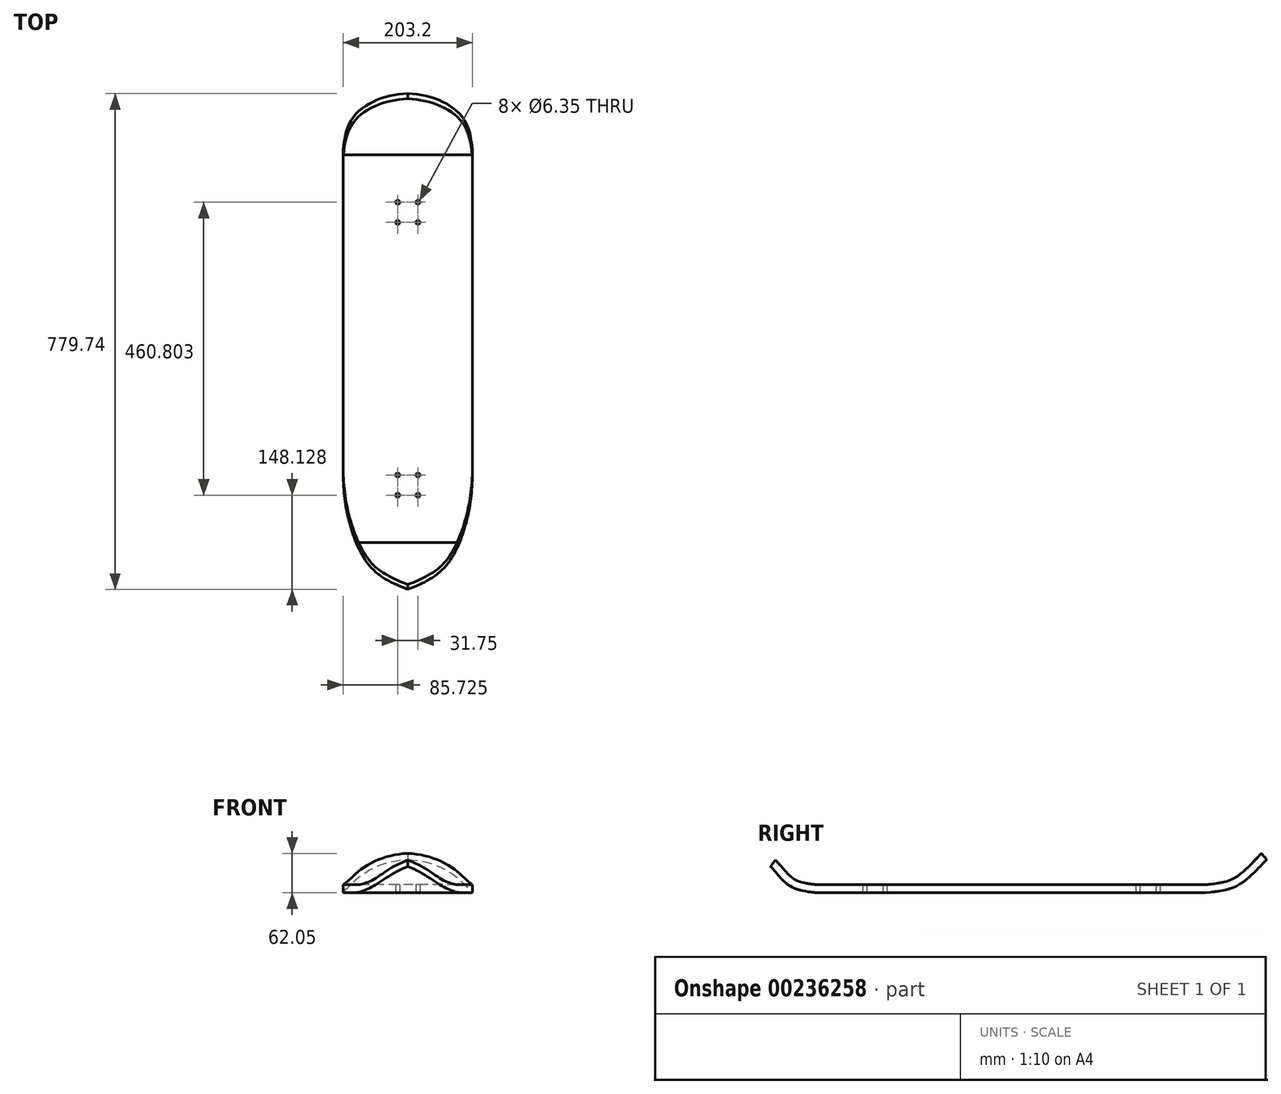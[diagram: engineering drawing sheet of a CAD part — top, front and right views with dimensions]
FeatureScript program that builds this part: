
annotation { "Feature Type Name" : "Feature", "Feature Type Description" : "" }
export const myFeature = defineFeature(function(context is Context, id is Id, definition is map)
    precondition{}
    {
        {
            var Q0;
            Q0=qCreatedBy(makeId("Top.planeOp"),FACE);
            var sketch = newSketch(context, id + "F0", { "sketchPlane" : qUnion([Q0])});
            skLineSegment(sketch, "E0.bottom", {"start": v(101.6, -304.8) * mm, "end": v(-101.6, -304.8) * mm});
            skLineSegment(sketch, "E0.top", {"start": v(101.6, 304.8) * mm, "end": v(-101.6, 304.8) * mm});
            skLineSegment(sketch, "E0.left", {"start": v(101.6, -304.8) * mm, "end": v(101.6, 304.8) * mm});
            skLineSegment(sketch, "E0.right", {"start": v(-101.6, -304.8) * mm, "end": v(-101.6, 304.8) * mm});
            skPoint(sketch, "E0.middle", {"position": v(0, 0) * mm});
            skPoint(sketch, "E1.middle", {"position": v(0, 214.53) * mm});
            skCircle(sketch, "E2", {"center": v(-15.87, 230.4) * mm, "radius": 3.18 * mm});
            skCircle(sketch, "E3", {"center": v(15.88, 230.4) * mm, "radius": 3.18 * mm});
            skCircle(sketch, "E4", {"center": v(-15.87, 198.65) * mm, "radius": 3.18 * mm});
            skCircle(sketch, "E5", {"center": v(15.88, 198.65) * mm, "radius": 3.18 * mm});
            skPoint(sketch, "E1.left.end.orphan", {"position": v(25.4, 239.93) * mm});
            skPoint(sketch, "E1.bottom.start.orphan", {"position": v(25.4, 189.13) * mm});
            skPoint(sketch, "E1.right.end.orphan", {"position": v(-25.4, 239.93) * mm});
            skPoint(sketch, "E1.right.start.orphan", {"position": v(-25.4, 189.13) * mm});
            skCircle(sketch, "E6.MirrorC", {"center": v(-15.87, -230.4) * mm, "radius": 3.18 * mm});
            skCircle(sketch, "E7.MirrorC", {"center": v(15.88, -230.4) * mm, "radius": 3.18 * mm});
            skCircle(sketch, "E8.MirrorC", {"center": v(15.88, -198.65) * mm, "radius": 3.18 * mm});
            skCircle(sketch, "E9.MirrorC", {"center": v(-15.87, -198.65) * mm, "radius": 3.18 * mm});
            skSolve(sketch);
        }
        {
            var Q0;
            Q0 = qSketchRegion(id + "F0", true);
            extrude(context, id + "F1", {"entities" : qUnion([Q0]), "endBound" : BoundingType.SYMMETRIC, "depth" : 12.7 * mm});
        }
        {
            var Q0;
            Q0=qCreatedBy(makeId("Right.planeOp"),FACE);
            var sketch = newSketch(context, id + "F2", { "sketchPlane" : qUnion([Q0])});
            skFitSpline(sketch, "E10", {"points": [v(307, 0) * mm, v(345.52, 7.4) * mm, v(371.6, 24.6) * mm, v(398.86, 52.45) * mm], "startDerivative": vector(118.45, 13.48) * mm, "endDerivative": vector(79.27, 85.49) * mm});
            skFitSpline(sketch, "E11", {"points": [v(-305.88, 0) * mm, v(-343.3, 8.85) * mm, v(-366.09, 30.81) * mm, v(-392.12, 56.85) * mm], "startDerivative": vector(-118.16, 13.66) * mm, "endDerivative": vector(-80.29, 75.77) * mm});
            skSolve(sketch);
        }
        {
            var Q0;
            Q0=makeQuery(id+"F1.opExtrude","SWEPT_FACE",FACE,{"disambiguationData":[OSD([sQuery(id+"F0.wireOp",EDGE,"E0.top")])]});
            var Q1;
            Q1=sQuery(id+"F2.wireOp",EDGE,"E10");
            sweep(context, id + "F3", {"operationType" : NewBodyOperationType.ADD, "profiles" : qUnion([Q0]), "path" : qUnion([Q1])});
        }
        {
            var Q0;
            Q0=makeQuery(id+"F1.opExtrude","SWEPT_FACE",FACE,{"disambiguationData":[OSD([sQuery(id+"F0.wireOp",EDGE,"E0.bottom")])]});
            var Q1;
            Q1=sQuery(id+"F2.wireOp",EDGE,"E11");
            sweep(context, id + "F4", {"operationType" : NewBodyOperationType.ADD, "profiles" : qUnion([Q0]), "path" : qUnion([Q1])});
        }
        {
            var Q0;
            Q0=makeQuery(id+"F4.opSweep","CAP_EDGE",EDGE,{"disambiguationData":[OSD([sQuery(id+"F0.wireOp",EDGE,"E0.bottom"),sQuery(id+"F0.wireOp",EDGE,"E0.left"),sQuery(id+"F2.wireOp",VERTEX,"E11.end")])],"isStart":false});
            var Q1;
            Q1=makeQuery(id+"F4.opSweep","CAP_EDGE",EDGE,{"disambiguationData":[OSD([sQuery(id+"F0.wireOp",EDGE,"E0.bottom"),sQuery(id+"F0.wireOp",EDGE,"E0.right"),sQuery(id+"F2.wireOp",VERTEX,"E11.end")])],"isStart":false});
            fillet(context, id + "F5", {"entities" : qUnion([Q0, Q1]), "radius" : 192.55 * mm, "tangentPropagation" : true, "allowEdgeOverflow" : false});
        }
        {
            var Q0;
            Q0=makeQuery(id+"F3.opSweep","CAP_EDGE",EDGE,{"disambiguationData":[OSD([sQuery(id+"F0.wireOp",EDGE,"E0.top"),sQuery(id+"F0.wireOp",EDGE,"E0.right"),sQuery(id+"F2.wireOp",VERTEX,"E10.end")])],"isStart":false});
            var Q1;
            Q1=makeQuery(id+"F3.opSweep","CAP_EDGE",EDGE,{"disambiguationData":[OSD([sQuery(id+"F0.wireOp",EDGE,"E0.top"),sQuery(id+"F0.wireOp",EDGE,"E0.left"),sQuery(id+"F2.wireOp",VERTEX,"E10.end")])],"isStart":false});
            fillet(context, id + "F6", {"entities" : qUnion([Q0, Q1]), "radius" : 107.93 * mm, "tangentPropagation" : true, "allowEdgeOverflow" : false});
        }
    });
